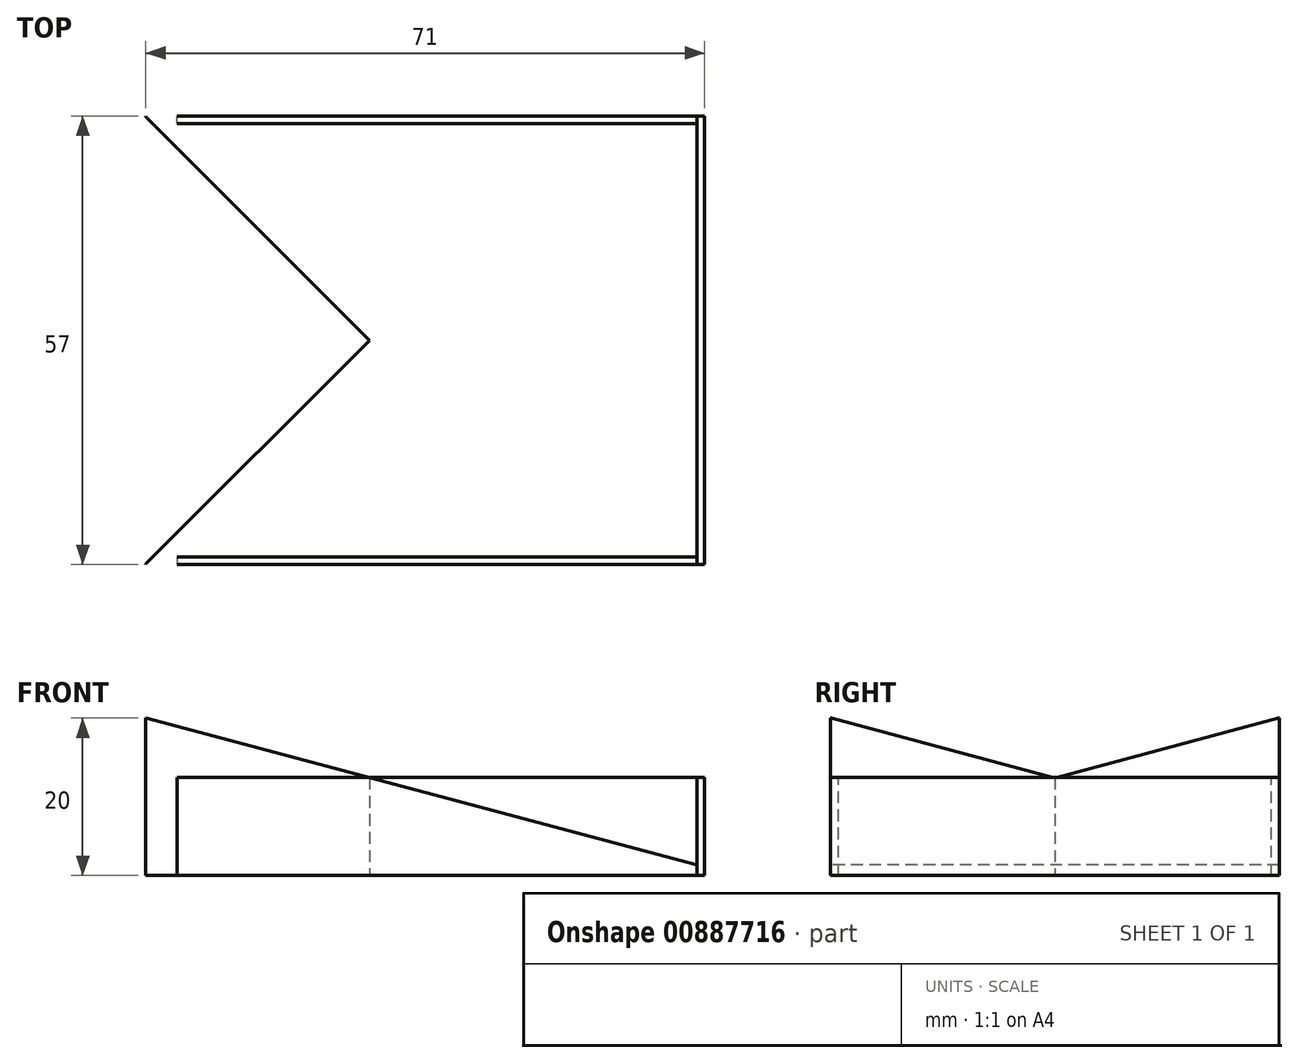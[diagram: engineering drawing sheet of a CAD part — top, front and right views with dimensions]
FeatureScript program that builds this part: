
annotation { "Feature Type Name" : "Feature", "Feature Type Description" : "" }
export const myFeature = defineFeature(function(context is Context, id is Id, definition is map)
    precondition{}
    {
        {
            var Q0;
            Q0=qCreatedBy(makeId("Front.planeOp"),FACE);
            var sketch = newSketch(context, id + "F0", { "sketchPlane" : qUnion([Q0])});
            skLineSegment(sketch, "E0", {"start": v(0, 0) * mm, "end": v(0, 1.34) * mm});
            skLineSegment(sketch, "E1", {"start": v(0, 1.34) * mm, "end": v(-70, 20) * mm});
            skLineSegment(sketch, "E2", {"start": v(-70, 20) * mm, "end": v(-70, 0) * mm});
            skLineSegment(sketch, "E3", {"start": v(-70, 0) * mm, "end": v(0, 0) * mm});
            skSolve(sketch);
        }
        {
            var Q0;
            Q0=makeQuery(id+"F0.imprint","IMPRINT",FACE,{"disambiguationData":[TD([[makeQuery(id+"F0.imprint","IMPRINT",EDGE,{"derivedFrom":sQuery(id+"F0.wireOp",EDGE,"E0")}),1.0]])]});
            var Q1;
            Q1=makeQuery(id+"F9dF8rJISVQHpEc_0.imprint","IMPRINT",FACE,{"disambiguationData":[TD([[makeQuery(id+"F9dF8rJISVQHpEc_0.imprint","IMPRINT",EDGE,{"derivedFrom":sQuery(id+"F9dF8rJISVQHpEc_0.wireOp",EDGE,"qavadp9l-ODOv-dQ1O-l7AE-eNmZk7nAarR0.bottom")}),-1.0]])]});
            extrude(context, id + "F1", {"entities" : qUnion([Q0, Q1]), "oppositeDirection" : true, "depth" : 57 * mm, "offsetDistance" : 25 * mm});
        }
        {
            var Q0;
            Q0=qCreatedBy(makeId("Right.planeOp"),FACE);
            var sketch = newSketch(context, id + "F2", { "sketchPlane" : qUnion([Q0])});
            skLineSegment(sketch, "E4.bottom", {"start": v(0, 0) * mm, "end": v(57, 0) * mm});
            skLineSegment(sketch, "E4.top", {"start": v(0, 12.5) * mm, "end": v(57, 12.5) * mm});
            skLineSegment(sketch, "E4.left", {"start": v(0, 0) * mm, "end": v(0, 12.5) * mm});
            skLineSegment(sketch, "E4.right", {"start": v(57, 0) * mm, "end": v(57, 12.5) * mm});
            skSolve(sketch);
        }
        {
            var Q0;
            Q0=makeQuery(id+"F2.imprint","IMPRINT",FACE,{"disambiguationData":[TD([[makeQuery(id+"F2.imprint","IMPRINT",EDGE,{"derivedFrom":sQuery(id+"F2.wireOp",EDGE,"E4.bottom")}),1.0]])]});
            extrude(context, id + "F3", {"entities" : qUnion([Q0]), "depth" : 1 * mm, "offsetDistance" : 25 * mm});
        }
        {
            var Q0;
            Q0=qCreatedBy(makeId("Front.planeOp"),FACE);
            var sketch = newSketch(context, id + "F4", { "sketchPlane" : qUnion([Q0])});
            skLineSegment(sketch, "E5.bottom", {"start": v(0, 0) * mm, "end": v(-66, 0) * mm});
            skLineSegment(sketch, "E5.top", {"start": v(0, 12.5) * mm, "end": v(-66, 12.5) * mm});
            skLineSegment(sketch, "E5.left", {"start": v(0, 0) * mm, "end": v(0, 12.5) * mm});
            skLineSegment(sketch, "E5.right", {"start": v(-66, 0) * mm, "end": v(-66, 12.5) * mm});
            skSolve(sketch);
        }
        {
            var Q0;
            Q0=makeQuery(id+"F4.imprint","IMPRINT",FACE,{"disambiguationData":[TD([[makeQuery(id+"F4.imprint","IMPRINT",EDGE,{"derivedFrom":sQuery(id+"F4.wireOp",EDGE,"E5.bottom")}),-1.0]])]});
            extrude(context, id + "F5", {"entities" : qUnion([Q0]), "oppositeDirection" : true, "depth" : 1 * mm, "offsetDistance" : 25 * mm});
        }
        {
            var Q0;
            Q0=makeQuery(id+"F1.opExtrude","CAP_FACE",FACE,{"disambiguationData":[OSD([sQuery(id+"F0.wireOp",EDGE,"E0"),sQuery(id+"F0.wireOp",EDGE,"E1"),sQuery(id+"F0.wireOp",EDGE,"E2"),sQuery(id+"F0.wireOp",EDGE,"E3")])],"isStart":false});
            cPlane(context, id + "F6", {"entities" : qUnion([Q0]), "cplaneType" : CPlaneType.OFFSET, "offset" : 0 * mm, "width" : 150 * mm, "height" : 150 * mm});
        }
        {
            var Q0;
            Q0=qCreatedBy(id+"F6.planeOp",FACE);
            var sketch = newSketch(context, id + "F7", { "sketchPlane" : qUnion([Q0])});
            skLineSegment(sketch, "E6.bottom", {"start": v(0, 0) * mm, "end": v(66, 0) * mm});
            skLineSegment(sketch, "E6.top", {"start": v(0, 12.5) * mm, "end": v(66, 12.5) * mm});
            skLineSegment(sketch, "E6.left", {"start": v(0, 0) * mm, "end": v(0, 12.5) * mm});
            skLineSegment(sketch, "E6.right", {"start": v(66, 0) * mm, "end": v(66, 12.5) * mm});
            skSolve(sketch);
        }
        {
            var Q0;
            Q0=makeQuery(id+"F7.imprint","IMPRINT",FACE,{"disambiguationData":[TD([[makeQuery(id+"F7.imprint","IMPRINT",EDGE,{"derivedFrom":sQuery(id+"F7.wireOp",EDGE,"E6.bottom")}),1.0]])]});
            extrude(context, id + "F8", {"entities" : qUnion([Q0]), "oppositeDirection" : true, "depth" : 1 * mm, "offsetDistance" : 25 * mm});
        }
        {
            var Q0;
            Q0=qCreatedBy(makeId("Top.planeOp"),FACE);
            var sketch = newSketch(context, id + "F9", { "sketchPlane" : qUnion([Q0])});
            skLineSegment(sketch, "E7", {"start": v(-70.06, 0) * mm, "end": v(-70.06, 57) * mm});
            skLineSegment(sketch, "E8", {"start": v(-70.06, 57) * mm, "end": v(-41.56, 28.5) * mm});
            skLineSegment(sketch, "E9", {"start": v(-41.56, 28.5) * mm, "end": v(-70.06, 0) * mm});
            skSolve(sketch);
        }
        {
            var Q0;
            Q0=makeQuery(id+"F9.imprint","IMPRINT",FACE,{"disambiguationData":[TD([[makeQuery(id+"F9.imprint","IMPRINT",EDGE,{"derivedFrom":sQuery(id+"F9.wireOp",EDGE,"E7")}),-1.0]])]});
            extrude(context, id + "F10", {"entities" : qUnion([Q0]), "operationType" : NewBodyOperationType.REMOVE, "depth" : 25 * mm, "offsetDistance" : 25 * mm});
        }
    });
